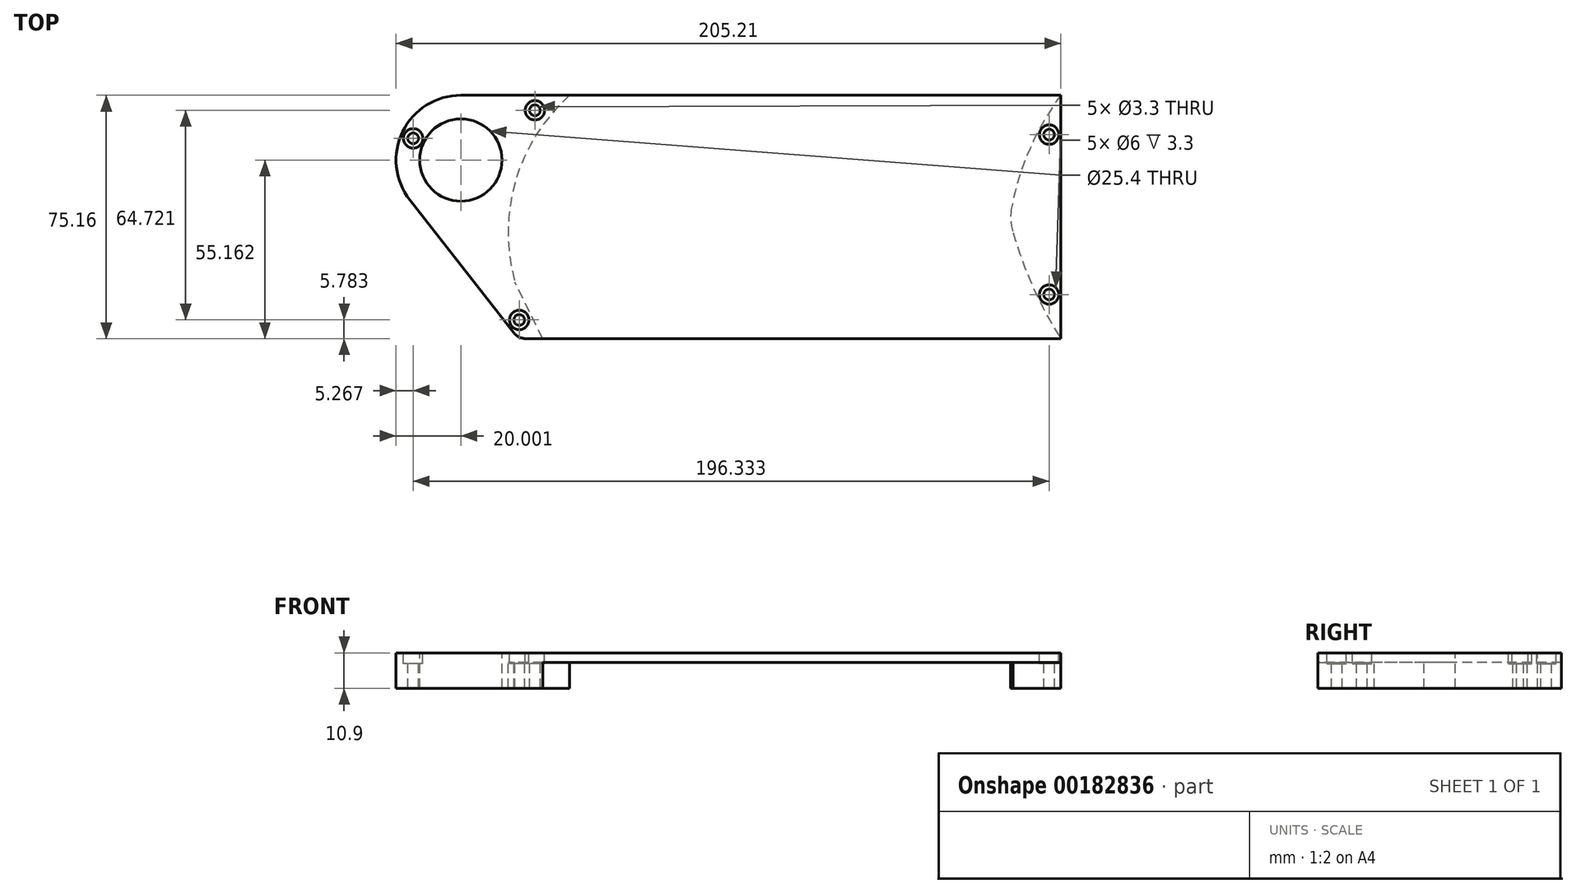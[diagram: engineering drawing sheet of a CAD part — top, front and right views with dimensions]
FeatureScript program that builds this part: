
annotation { "Feature Type Name" : "Feature", "Feature Type Description" : "" }
export const myFeature = defineFeature(function(context is Context, id is Id, definition is map)
    precondition{}
    {
        {
            var Q0;
            Q0=qCreatedBy(makeId("Top.planeOp"),FACE);
            var sketch = newSketch(context, id + "F0", { "sketchPlane" : qUnion([Q0])});
            skLineSegment(sketch, "E0", {"start": v(86, 37.87) * mm, "end": v(-99.2, 37.87) * mm});
            skLineSegment(sketch, "E1", {"start": v(86, -37.29) * mm, "end": v(-81.47, -37.29) * mm});
            skLineSegment(sketch, "E2.0", {"start": v(86, -37.29) * mm, "end": v(86, 37.87) * mm});
            skArc(sketch, "E3", {"start": v(70.84, 3.43) * mm, "mid": v(70.55, -0.57) * mm, "end": v(71.29, -4.5) * mm});
            skLineSegment(sketch, "E4", {"start": v(-73.97, -37.29) * mm, "end": v(-82.52, -19.87) * mm});
            skArc(sketch, "E5", {"start": v(-65.62, 37.87) * mm, "mid": v(-82.32, 11.42) * mm, "end": v(-82.52, -19.87) * mm});
            skArc(sketch, "E6", {"start": v(71.29, -4.5) * mm, "mid": v(77.46, -21.43) * mm, "end": v(86, -37.29) * mm});
            skCircle(sketch, "E7", {"center": v(-99.2, 17.87) * mm, "radius": 12.7 * mm});
            skLineSegment(sketch, "E8", {"start": v(-81.47, -37.29) * mm, "end": v(-114.97, 5.55) * mm});
            skArc(sketch, "E9", {"start": v(-99.2, 37.87) * mm, "mid": v(-117.19, 26.64) * mm, "end": v(-114.97, 5.55) * mm});
            skPoint(sketch, "E10.orphan", {"position": v(-70.88, 32.5) * mm});
            skLineSegment(sketch, "E11", {"start": v(-73.97, -37.29) * mm, "end": v(-73.97, -48.25) * mm});
            skArc(sketch, "E12", {"start": v(86, 37.87) * mm, "mid": v(76.52, 21.49) * mm, "end": v(70.84, 3.43) * mm});
            skSolve(sketch);
        }
        {
            var Q0;
            {var subQ4=sQuery(id+"F0.wireOp",EDGE,"E4");Q0=makeQuery(id+"F0.imprint","IMPRINT",FACE,{"disambiguationData":[TD([[makeQuery(id+"F0.imprint","IMPRINT",EDGE,{"derivedFrom":subQ4}),1.0]])]});}
            var Q1;
            {var subQ0=sQuery(id+"F0.wireOp",EDGE,"A3gzjdv7-mEnE-012z-8kgW-jsFch6enEW4N");Q1=makeQuery(id+"F0.imprint","IMPRINT",FACE,{"disambiguationData":[TD([[makeQuery(id+"F0.imprint","IMPRINT",EDGE,{"derivedFrom":subQ0}),1.0]])]});}
            var Q2;
            Q2=makeQuery(id+"F0.imprint","IMPRINT",FACE,{"disambiguationData":[TD([[makeQuery(id+"F0.imprint","IMPRINT",EDGE,{"derivedFrom":sQuery(id+"F0.wireOp",EDGE,"E2.0")}),1.0]])]});
            extrude(context, id + "F1", {"entities" : qUnion([Q0, Q1, Q2]), "oppositeDirection" : true, "depth" : 7.9 * mm});
        }
        {
            var Q0;
            Q0=makeQuery(id+"F0.imprint","IMPRINT",FACE,{"disambiguationData":[TD([[makeQuery(id+"F0.imprint","IMPRINT",EDGE,{"derivedFrom":sQuery(id+"F0.wireOp",EDGE,"E3")}),-1.0]])]});
            var Q1;
            Q1=makeQuery(id+"F1.opExtrude","CAP_FACE",FACE,{"disambiguationData":[OSD([sQuery(id+"F0.wireOp",EDGE,"E0"),sQuery(id+"F0.wireOp",EDGE,"E1"),sQuery(id+"F0.wireOp",EDGE,"E4"),sQuery(id+"F0.wireOp",EDGE,"E5"),sQuery(id+"F0.wireOp",EDGE,"E7"),sQuery(id+"F0.wireOp",EDGE,"E8"),sQuery(id+"F0.wireOp",EDGE,"E9"),sQuery(id+"F0.wireOp",EDGE,"A3gzjdv7-mEnE-012z-8kgW-jsFch6enEW4N"),sQuery(id+"F0.wireOp",EDGE,"hQGAswSE-0Ler-CEZg-wxhm-4HyRDI8fAloK"),sQuery(id+"F0.wireOp",EDGE,"pylyCLkE-LzyG-ncyl-YxF8-dlpm6YxqzSpV")])],"isStart":true});
            extrude(context, id + "F2", {"entities" : qUnion([Q0, Q1]), "operationType" : NewBodyOperationType.ADD, "depth" : 3 * mm});
        }
        {
            var Q0;
            Q0=makeQuery(id+"F0.imprint","IMPRINT",FACE,{"disambiguationData":[TD([[makeQuery(id+"F0.imprint","IMPRINT",EDGE,{"derivedFrom":sQuery(id+"F0.wireOp",EDGE,"E2.0")}),1.0]])]});
            extrude(context, id + "F3", {"entities" : qUnion([Q0]), "depth" : 3 * mm});
        }
        {
            var Q0;
            {var subQ0=sQuery(id+"F0.wireOp",EDGE,"E8");var subQ1=sQuery(id+"F0.wireOp",EDGE,"E1");Q0=makeQuery(id+"F2.boolean.opBoolean","MERGE",EDGE,{"derivedFrom":[makeQuery(id+"F1.opExtrude","SWEPT_EDGE",EDGE,{"disambiguationData":[OSD([subQ1,subQ0])]}),makeQuery(id+"F2.opExtrude","SWEPT_EDGE",EDGE,{"disambiguationData":[OSD([subQ1,subQ0])]})]});}
            fillet(context, id + "F4", {"entities" : qUnion([Q0]), "radius" : 5 * mm, "tangentPropagation" : true, "allowEdgeOverflow" : false});
        }
        {
            var Q0;
            {var subQ0=sQuery(id+"F0.wireOp",EDGE,"pylyCLkE-LzyG-ncyl-YxF8-dlpm6YxqzSpV");var subQ1=sQuery(id+"F0.wireOp",EDGE,"hQGAswSE-0Ler-CEZg-wxhm-4HyRDI8fAloK");var subQ2=sQuery(id+"F0.wireOp",EDGE,"E7");var subQ3=sQuery(id+"F0.wireOp",EDGE,"E5");var subQ4=sQuery(id+"F0.wireOp",EDGE,"E4");var subQ5=sQuery(id+"F0.wireOp",EDGE,"E1");var subQ6=sQuery(id+"F0.wireOp",EDGE,"E0");Q0=makeQuery(id+"F2P3khQRtNti67P_0.boolean.opBoolean","MERGE",FACE,{"derivedFrom":[makeQuery(id+"F2.boolean.opBoolean","MERGE",FACE,{"derivedFrom":[makeQuery(id+"F2.opExtrude","CAP_FACE",FACE,{"disambiguationData":[OSD([subQ6,subQ5,sQuery(id+"F0.wireOp",EDGE,"E3"),subQ4,subQ3,sQuery(id+"F0.wireOp",EDGE,"E6"),sQuery(id+"F0.wireOp",EDGE,"E12")])],"isStart":false}),makeQuery(id+"F2.opExtrude","CAP_FACE",FACE,{"disambiguationData":[OSD([subQ6,subQ5,subQ4,subQ3,subQ2,sQuery(id+"F0.wireOp",EDGE,"E8"),sQuery(id+"F0.wireOp",EDGE,"E9"),sQuery(id+"F0.wireOp",EDGE,"A3gzjdv7-mEnE-012z-8kgW-jsFch6enEW4N"),subQ1,subQ0])],"isStart":false})]}),makeQuery(id+"F2P3khQRtNti67P_0.opExtrude","CAP_FACE",FACE,{"disambiguationData":[OSD([subQ2,sQuery(id+"F0.wireOp",EDGE,"ieWmS8p1-3MAB-9NXB-6I7M-OzDbltPEcY0O"),subQ1,subQ0])],"isStart":false})]});}
            var sketch = newSketch(context, id + "F5", { "sketchPlane" : qUnion([Q0])});
            skSolve(sketch);
        }
        {
            var Q0;
            Q0=makeQuery(id+"F1.opExtrude","SWEPT_BODY",BODY,{"disambiguationData":[OSD([sQuery(id+"F0.wireOp",EDGE,"E0"),sQuery(id+"F0.wireOp",EDGE,"E1"),sQuery(id+"F0.wireOp",EDGE,"E4"),sQuery(id+"F0.wireOp",EDGE,"E5"),sQuery(id+"F0.wireOp",EDGE,"E7"),sQuery(id+"F0.wireOp",EDGE,"E8"),sQuery(id+"F0.wireOp",EDGE,"E9"),sQuery(id+"F0.wireOp",EDGE,"A3gzjdv7-mEnE-012z-8kgW-jsFch6enEW4N"),sQuery(id+"F0.wireOp",EDGE,"hQGAswSE-0Ler-CEZg-wxhm-4HyRDI8fAloK"),sQuery(id+"F0.wireOp",EDGE,"pylyCLkE-LzyG-ncyl-YxF8-dlpm6YxqzSpV")])]});
            var Q1;
            Q1=makeQuery(id+"F1.opExtrude","SWEPT_BODY",BODY,{"disambiguationData":[OSD([sQuery(id+"F0.wireOp",EDGE,"E2.0"),sQuery(id+"F0.wireOp",EDGE,"E3"),sQuery(id+"F0.wireOp",EDGE,"E6"),sQuery(id+"F0.wireOp",EDGE,"E12")])]});
            var Q2;
            Q2=makeQuery(id+"F3.opExtrude","SWEPT_BODY",BODY,{"disambiguationData":[OSD([sQuery(id+"F0.wireOp",EDGE,"E2.0"),sQuery(id+"F0.wireOp",EDGE,"E3"),sQuery(id+"F0.wireOp",EDGE,"E6"),sQuery(id+"F0.wireOp",EDGE,"E12")])]});
            booleanBodies(context, id + "F6", {"operationType" : BooleanOperationType.UNION, "tools" : qUnion([Q0, Q1, Q2])});
        }
        {
            var Q0;
            {var subQ9=sQuery(id+"F0.wireOp",EDGE,"E3");Q0=makeQuery(id+"F5.imprint","IMPRINT",FACE,{"disambiguationData":[TD([[makeQuery(id+"F5.imprint","IMPRINT",EDGE,{"derivedFrom":makeQuery(id+"F2.opExtrude","CAP_EDGE",EDGE,{"disambiguationData":[OSD([subQ9])],"isStart":false})}),-1.0]])]});}
            var sketch = newSketch(context, id + "F7", { "sketchPlane" : qUnion([Q0])});
            skPoint(sketch, "E13", {"position": v(-76.36, 33.21) * mm});
            skPoint(sketch, "E14", {"position": v(82.39, 25.7) * mm});
            skPoint(sketch, "E15", {"position": v(82.39, -23.67) * mm});
            skPoint(sketch, "E16", {"position": v(-81.2, -31.5) * mm});
            skPoint(sketch, "E17", {"position": v(-113.94, 24.55) * mm});
            skSolve(sketch);
        }
        {
            var Q0;
            Q0=sQuery(id+"F7.wireOp",VERTEX,"E13");
            var Q1;
            Q1=sQuery(id+"F7.wireOp",VERTEX,"E17");
            var Q2;
            Q2=sQuery(id+"F7.wireOp",VERTEX,"E16");
            var Q3;
            Q3=sQuery(id+"F7.wireOp",VERTEX,"E15");
            var Q4;
            Q4=sQuery(id+"F7.wireOp",VERTEX,"E14");
            var Q5;
            Q5=makeQuery(id+"F1.opExtrude","SWEPT_BODY",BODY,{"disambiguationData":[OSD([sQuery(id+"F0.wireOp",EDGE,"E0"),sQuery(id+"F0.wireOp",EDGE,"E1"),sQuery(id+"F0.wireOp",EDGE,"E4"),sQuery(id+"F0.wireOp",EDGE,"E5"),sQuery(id+"F0.wireOp",EDGE,"E7"),sQuery(id+"F0.wireOp",EDGE,"E8"),sQuery(id+"F0.wireOp",EDGE,"E9")])]});
            hole(context, id + "F8", {"style" : HoleStyle.C_BORE, "endStyle" : HoleEndStyle.THROUGH, "holeDiameter" : 3.3 * mm, "cBoreDiameter" : 6 * mm, "cBoreDepth" : 3.3 * mm, "startFromSketch" : true, "locations" : qUnion([Q0, Q1, Q2, Q3, Q4]), "scope" : qUnion([Q5]), "isTappedThrough" : true});
        }
    });
